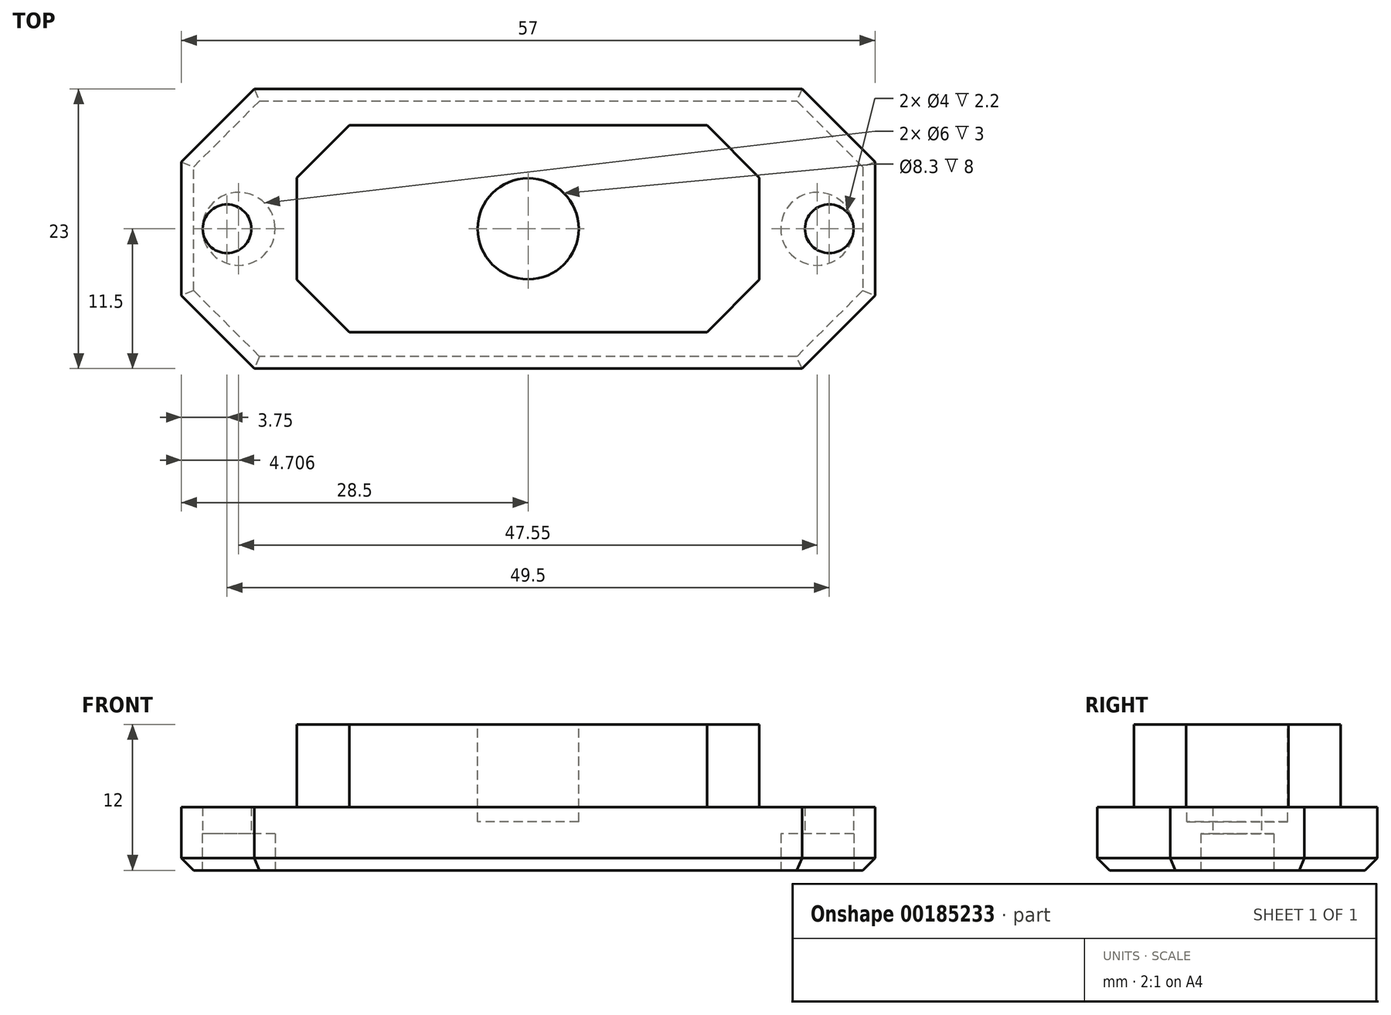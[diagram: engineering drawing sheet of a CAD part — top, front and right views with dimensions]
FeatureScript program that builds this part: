
annotation { "Feature Type Name" : "Feature", "Feature Type Description" : "" }
export const myFeature = defineFeature(function(context is Context, id is Id, definition is map)
    precondition{}
    {
        {
            var Q0;
            Q0=qCreatedBy(makeId("Top.planeOp"),FACE);
            var sketch = newSketch(context, id + "F0", { "sketchPlane" : qUnion([Q0])});
            skLineSegment(sketch, "E0.bottom", {"start": v(-14.7, 8.5) * mm, "end": v(14.7, 8.5) * mm});
            skLineSegment(sketch, "E0.top", {"start": v(-14.7, -8.5) * mm, "end": v(14.7, -8.5) * mm});
            skLineSegment(sketch, "E0.left", {"start": v(-19, 4.2) * mm, "end": v(-19, -4.2) * mm});
            skLineSegment(sketch, "E0.right", {"start": v(19, 4.2) * mm, "end": v(19, -4.2) * mm});
            skLineSegment(sketch, "E1.bottom", {"start": v(-22.5, 11.5) * mm, "end": v(22.5, 11.5) * mm});
            skLineSegment(sketch, "E1.top", {"start": v(-22.5, -11.5) * mm, "end": v(22.5, -11.5) * mm});
            skLineSegment(sketch, "E1.left", {"start": v(-28.5, 5.5) * mm, "end": v(-28.5, -5.5) * mm});
            skLineSegment(sketch, "E1.right", {"start": v(28.5, 5.5) * mm, "end": v(28.5, -5.5) * mm});
            skCircle(sketch, "E2", {"center": v(-24.75, 0) * mm, "radius": 2 * mm});
            skCircle(sketch, "E3.MirrorC", {"center": v(24.75, 0) * mm, "radius": 2 * mm});
            skLineSegment(sketch, "E4", {"start": v(-14.7, 8.5) * mm, "end": v(-19, 4.2) * mm});
            skLineSegment(sketch, "E5.MirrorCS", {"start": v(14.7, 8.5) * mm, "end": v(19, 4.2) * mm});
            skLineSegment(sketch, "E6.MirrorCS", {"start": v(-14.7, -8.5) * mm, "end": v(-19, -4.2) * mm});
            skLineSegment(sketch, "E7.MirrorCS", {"start": v(14.7, -8.5) * mm, "end": v(19, -4.2) * mm});
            skLineSegment(sketch, "E8", {"start": v(-28.5, 5.5) * mm, "end": v(-22.5, 11.5) * mm});
            skLineSegment(sketch, "E9.MirrorCS", {"start": v(28.5, 5.5) * mm, "end": v(22.5, 11.5) * mm});
            skLineSegment(sketch, "E10.MirrorCS", {"start": v(-28.5, -5.5) * mm, "end": v(-22.5, -11.5) * mm});
            skLineSegment(sketch, "E11.MirrorCS", {"start": v(28.5, -5.5) * mm, "end": v(22.5, -11.5) * mm});
            skPoint(sketch, "E12.orphan", {"position": v(-28.5, 11.5) * mm});
            skPoint(sketch, "E13.orphan", {"position": v(-19, 8.5) * mm});
            skSolve(sketch);
        }
        {
            var Q0;
            Q0=makeQuery(id+"F0.imprint","IMPRINT",FACE,{"disambiguationData":[TD([[makeQuery(id+"F0.imprint","IMPRINT",EDGE,{"derivedFrom":sQuery(id+"F0.wireOp",EDGE,"E0.bottom")}),-1.0]])]});
            extrude(context, id + "F1", {"entities" : qUnion([Q0]), "depth" : 12 * mm});
        }
        {
            var Q0;
            Q0=makeQuery(id+"F0.imprint","IMPRINT",FACE,{"disambiguationData":[TD([[makeQuery(id+"F0.imprint","IMPRINT",EDGE,{"derivedFrom":sQuery(id+"F0.wireOp",EDGE,"E0.bottom")}),1.0]])]});
            extrude(context, id + "F2", {"entities" : qUnion([Q0]), "operationType" : NewBodyOperationType.ADD, "depth" : 5.2 * mm});
        }
        {
            var Q0;
            Q0=makeQuery(id+"F2.opExtrude","CAP_EDGE",EDGE,{"disambiguationData":[OSD([sQuery(id+"F0.wireOp",EDGE,"E1.top")])],"isStart":true});
            var Q1;
            Q1=makeQuery(id+"F2.opExtrude","CAP_EDGE",EDGE,{"disambiguationData":[OSD([sQuery(id+"F0.wireOp",EDGE,"E10.MirrorCS")])],"isStart":true});
            var Q2;
            Q2=makeQuery(id+"F2.opExtrude","CAP_EDGE",EDGE,{"disambiguationData":[OSD([sQuery(id+"F0.wireOp",EDGE,"E1.left")])],"isStart":true});
            var Q3;
            Q3=makeQuery(id+"F2.opExtrude","CAP_EDGE",EDGE,{"disambiguationData":[OSD([sQuery(id+"F0.wireOp",EDGE,"E8")])],"isStart":true});
            var Q4;
            Q4=makeQuery(id+"F2.opExtrude","CAP_EDGE",EDGE,{"disambiguationData":[OSD([sQuery(id+"F0.wireOp",EDGE,"E1.bottom")])],"isStart":true});
            var Q5;
            Q5=makeQuery(id+"F2.opExtrude","CAP_EDGE",EDGE,{"disambiguationData":[OSD([sQuery(id+"F0.wireOp",EDGE,"E9.MirrorCS")])],"isStart":true});
            var Q6;
            Q6=makeQuery(id+"F2.opExtrude","CAP_EDGE",EDGE,{"disambiguationData":[OSD([sQuery(id+"F0.wireOp",EDGE,"E1.right")])],"isStart":true});
            var Q7;
            Q7=makeQuery(id+"F2.opExtrude","CAP_EDGE",EDGE,{"disambiguationData":[OSD([sQuery(id+"F0.wireOp",EDGE,"E11.MirrorCS")])],"isStart":true});
            chamfer(context, id + "F3", {"entities" : qUnion([Q0, Q1, Q2, Q3, Q4, Q5, Q6, Q7]), "width" : 1 * mm, "tangentPropagation" : true});
        }
        {
            var Q0;
            Q0=makeQuery(id+"F1.opExtrude","CAP_FACE",FACE,{"disambiguationData":[OSD([sQuery(id+"F0.wireOp",EDGE,"E0.bottom"),sQuery(id+"F0.wireOp",EDGE,"E0.top"),sQuery(id+"F0.wireOp",EDGE,"E0.left"),sQuery(id+"F0.wireOp",EDGE,"E0.right"),sQuery(id+"F0.wireOp",EDGE,"E4"),sQuery(id+"F0.wireOp",EDGE,"E5.MirrorCS"),sQuery(id+"F0.wireOp",EDGE,"E6.MirrorCS"),sQuery(id+"F0.wireOp",EDGE,"E7.MirrorCS")])],"isStart":false});
            var sketch = newSketch(context, id + "F4", { "sketchPlane" : qUnion([Q0])});
            skCircle(sketch, "E14", {"center": v(0, 0) * mm, "radius": 4.15 * mm});
            skSolve(sketch);
        }
        {
            var Q0;
            Q0=makeQuery(id+"F4.imprint","IMPRINT",FACE,{"disambiguationData":[TD([[makeQuery(id+"F4.imprint","IMPRINT",EDGE,{"derivedFrom":sQuery(id+"F4.wireOp",EDGE,"E14")}),1.0]])]});
            extrude(context, id + "F5", {"entities" : qUnion([Q0]), "operationType" : NewBodyOperationType.REMOVE, "oppositeDirection" : true, "depth" : 8 * mm});
        }
        {
            var Q0;
            Q0=qCreatedBy(makeId("Top.planeOp"),FACE);
            var sketch = newSketch(context, id + "F6", { "sketchPlane" : qUnion([Q0])});
            skCircle(sketch, "E15", {"center": v(-23.8, 0) * mm, "radius": 3 * mm});
            skCircle(sketch, "E16", {"center": v(23.76, 0) * mm, "radius": 3 * mm});
            skSolve(sketch);
        }
        {
            var Q0;
            Q0 = qSketchRegion(id + "F6", true);
            extrude(context, id + "F7", {"entities" : qUnion([Q0]), "operationType" : NewBodyOperationType.REMOVE, "depth" : 3 * mm});
        }
    });
